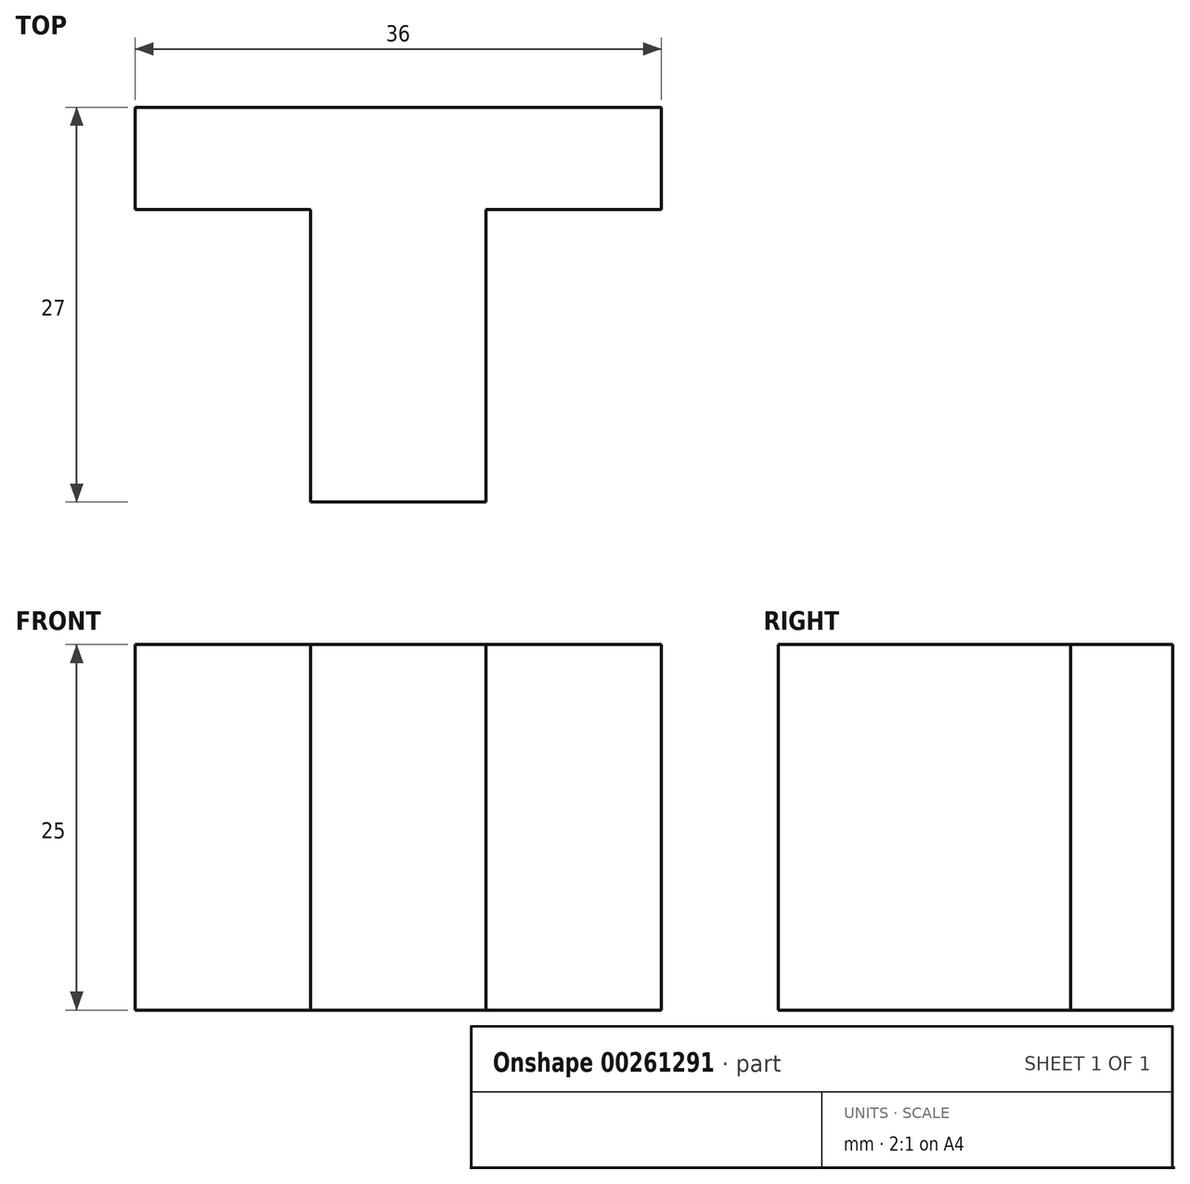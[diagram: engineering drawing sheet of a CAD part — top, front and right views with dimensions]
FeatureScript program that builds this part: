
annotation { "Feature Type Name" : "Feature", "Feature Type Description" : "" }
export const myFeature = defineFeature(function(context is Context, id is Id, definition is map)
    precondition{}
    {
        {
            var Q0;
            Q0=qCreatedBy(makeId("Top.planeOp"),FACE);
            var sketch = newSketch(context, id + "F0", { "sketchPlane" : qUnion([Q0])});
            skLineSegment(sketch, "E0", {"start": v(-4.11, 0) * mm, "end": v(7.89, 0) * mm});
            skLineSegment(sketch, "E1", {"start": v(7.89, 0) * mm, "end": v(7.89, 20) * mm});
            skLineSegment(sketch, "E2", {"start": v(7.89, 20) * mm, "end": v(19.89, 20) * mm});
            skLineSegment(sketch, "E3", {"start": v(19.89, 20) * mm, "end": v(19.89, 27) * mm});
            skLineSegment(sketch, "E4", {"start": v(19.89, 27) * mm, "end": v(-16.11, 27) * mm});
            skLineSegment(sketch, "E5", {"start": v(-4.11, 0) * mm, "end": v(-4.11, 20) * mm});
            skLineSegment(sketch, "E6", {"start": v(-4.11, 20) * mm, "end": v(-16.11, 20) * mm});
            skLineSegment(sketch, "E7", {"start": v(-16.11, 27) * mm, "end": v(-16.11, 20) * mm});
            skSolve(sketch);
        }
        {
            var Q0;
            Q0=makeQuery(id+"F0.imprint","IMPRINT",FACE,{"disambiguationData":[TD([[makeQuery(id+"F0.imprint","IMPRINT",EDGE,{"derivedFrom":sQuery(id+"F0.wireOp",EDGE,"E0")}),1.0]])]});
            extrude(context, id + "F1", {"entities" : qUnion([Q0]), "depth" : 25 * mm});
        }
    });
